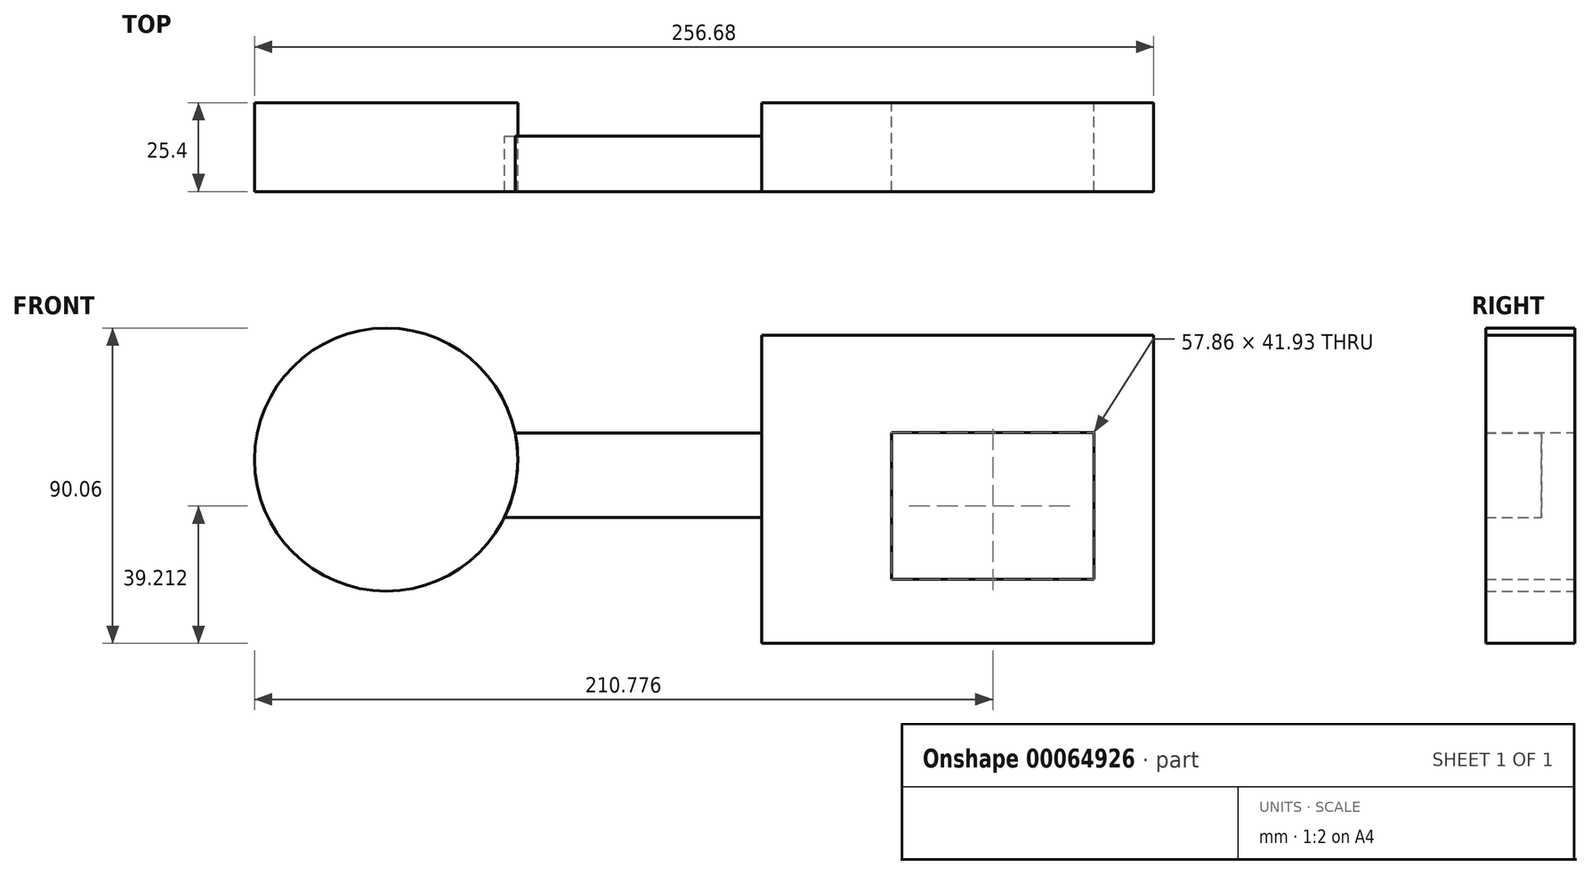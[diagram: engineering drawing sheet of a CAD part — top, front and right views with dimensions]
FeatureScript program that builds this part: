
annotation { "Feature Type Name" : "Feature", "Feature Type Description" : "" }
export const myFeature = defineFeature(function(context is Context, id is Id, definition is map)
    precondition{}
    {
        {
            var Q0;
            Q0=qCreatedBy(makeId("Front.planeOp"),FACE);
            var sketch = newSketch(context, id + "F0", { "sketchPlane" : qUnion([Q0])});
            skLineSegment(sketch, "E0.bottom", {"start": v(-57.48, 44.74) * mm, "end": v(54.4, 44.74) * mm});
            skLineSegment(sketch, "E0.top", {"start": v(-57.48, -43.32) * mm, "end": v(54.4, -43.32) * mm});
            skLineSegment(sketch, "E0.left", {"start": v(-57.48, 44.74) * mm, "end": v(-57.48, -43.32) * mm});
            skLineSegment(sketch, "E0.right", {"start": v(54.4, 44.74) * mm, "end": v(54.4, -43.32) * mm});
            skLineSegment(sketch, "E1.bottom", {"start": v(-20.44, 16.86) * mm, "end": v(37.42, 16.86) * mm});
            skLineSegment(sketch, "E1.top", {"start": v(-20.44, -25.07) * mm, "end": v(37.42, -25.07) * mm});
            skLineSegment(sketch, "E1.left", {"start": v(-20.44, 16.86) * mm, "end": v(-20.44, -25.07) * mm});
            skLineSegment(sketch, "E1.right", {"start": v(37.42, 16.86) * mm, "end": v(37.42, -25.07) * mm});
            skCircle(sketch, "E2", {"center": v(-164.71, 9.16) * mm, "radius": 37.58 * mm});
            skSolve(sketch);
        }
        {
            var Q0;
            Q0 = qSketchRegion(id + "F0", true);
            extrude(context, id + "F1", {"entities" : qUnion([Q0]), "depth" : 25.4 * mm});
        }
        {
            var Q0;
            Q0=makeQuery(id+"F1.opExtrude","SWEPT_FACE",FACE,{"disambiguationData":[OSD([sQuery(id+"F0.wireOp",EDGE,"E0.left")])]});
            var sketch = newSketch(context, id + "F2", { "sketchPlane" : qUnion([Q0])});
            skLineSegment(sketch, "E3.bottom", {"start": v(9.55, 16.76) * mm, "end": v(25.4, 16.76) * mm});
            skLineSegment(sketch, "E3.top", {"start": v(9.55, -7.32) * mm, "end": v(25.4, -7.32) * mm});
            skLineSegment(sketch, "E3.left", {"start": v(9.55, 16.76) * mm, "end": v(9.55, -7.32) * mm});
            skLineSegment(sketch, "E3.right", {"start": v(25.4, 16.76) * mm, "end": v(25.4, -7.32) * mm});
            skSolve(sketch);
        }
        {
            var Q0;
            Q0 = qSketchRegion(id + "F2", true);
            var Q1;
            Q1=makeQuery(id+"F1.opExtrude","SWEPT_FACE",FACE,{"disambiguationData":[OSD([sQuery(id+"F0.wireOp",EDGE,"E2")])]});
            var Q2;
            Q2=makeQuery(id+"F1.opExtrude","SWEPT_BODY",BODY,{"disambiguationData":[OSD([sQuery(id+"F0.wireOp",EDGE,"E2")])]});
            extrude(context, id + "F3", {"entities" : qUnion([Q0]), "endBound" : BoundingType.UP_TO_BODY, "endBoundEntityFace" : qUnion([Q1]), "endBoundEntityBody" : qUnion([Q2]), "depth" : 25.4 * mm});
        }
    });
